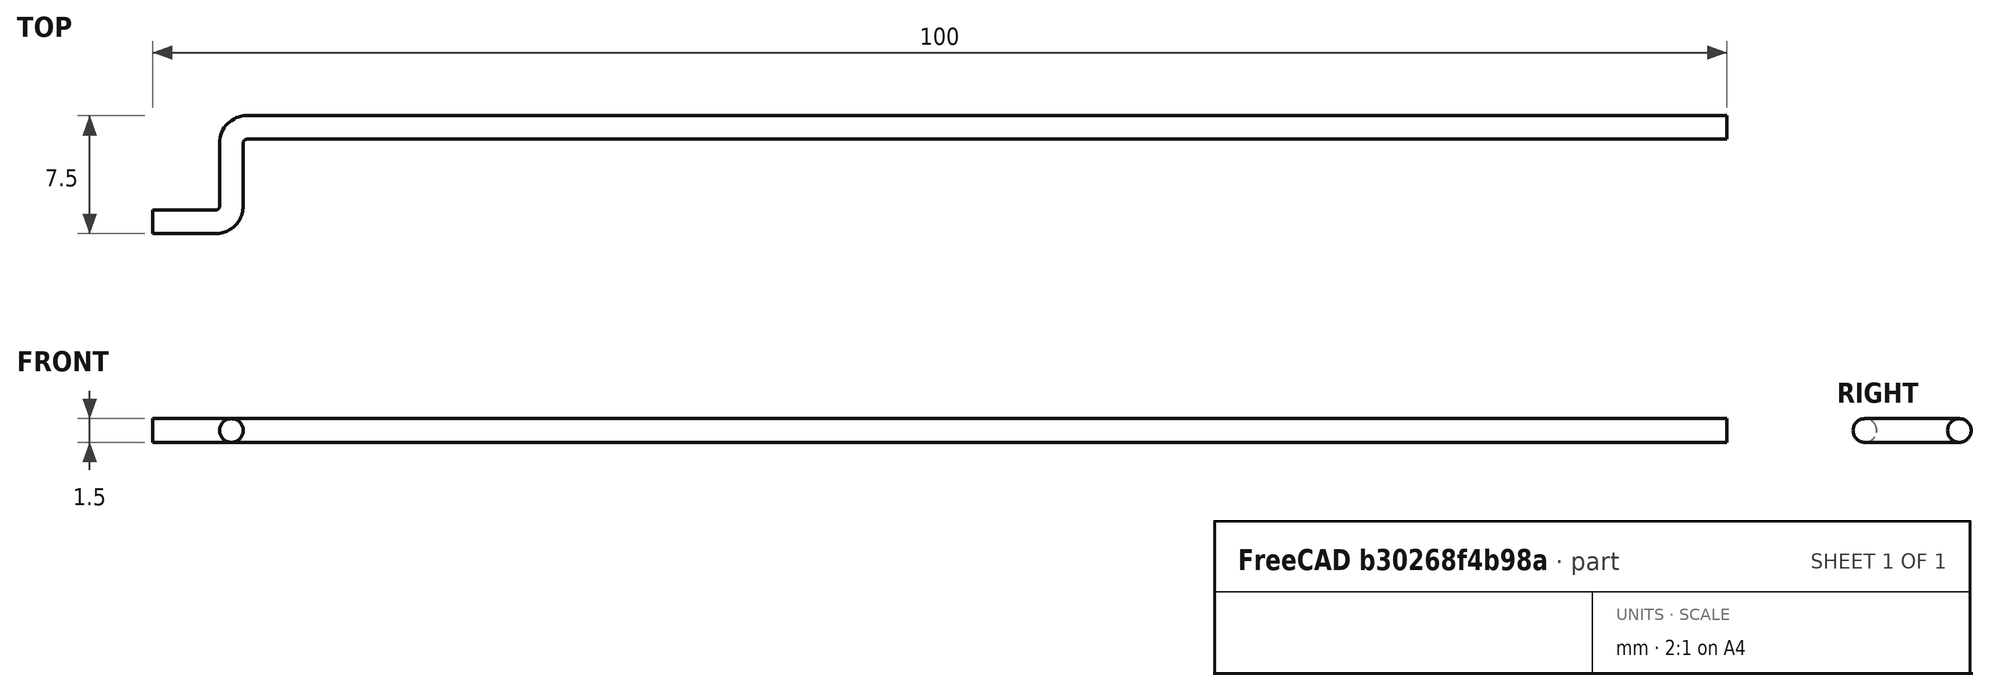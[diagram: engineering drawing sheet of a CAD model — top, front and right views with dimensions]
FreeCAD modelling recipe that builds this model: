
FCSTD DOCUMENT  (FreeCAD 0.15R4671 (Git))
Label: servo_rod_100mm
License: All rights reserved
LicenseURL: http://es.wikipedia.org/wiki/Todos_los_derechos_reservados
objects: Sketcher::SketchObject×2, Part::Sweep×1
note: 3 computed .brp shape members not serialized (recipe doc carries the construction recipe); baked Part::Feature solids carry a one-line shape summary decoded from their .brp

FEATURE [Sketcher::SketchObject] Sketch001  label="Sección"
  Placement = pos=(0,0,0) rot=(0.57735,0.57735,0.57735;2.0944rad)
  sketch-geometry (1):
    g0: Circle CenterX=0 CenterY=0 CenterZ=0 NormalX=0 NormalY=0 NormalZ=1 Radius=0.75
  constraints (2):
    c: Coincident(g0,g-1)
    c: Radius(g0) = 0.75
FEATURE [Sketcher::SketchObject] Sketch  label="Línea Varilla"
  sketch-geometry (5):
    g0: LineSegment StartX=0 StartY=0 StartZ=0 EndX=4 EndY=0 EndZ=0
    g1: LineSegment StartX=5 StartY=1 StartZ=0 EndX=5 EndY=5 EndZ=0
    g2: LineSegment StartX=6 StartY=6 StartZ=0 EndX=100 EndY=6 EndZ=0
    g3: ArcOfCircle CenterX=4 CenterY=1 CenterZ=0 NormalX=0 NormalY=0 NormalZ=1 Radius=1 StartAngle=4.71239 EndAngle=6.28319
    g4: ArcOfCircle CenterX=6 CenterY=5 CenterZ=0 NormalX=0 NormalY=0 NormalZ=1 Radius=1 StartAngle=1.5708 EndAngle=3.14159
  constraints (13):
    c: Coincident(g-1,g0)
    c: Horizontal(g0)
    c: Vertical(g1)
    c: Horizontal(g2)
    c: Tangent(g1,g3) = -1.5708
    c: Tangent(g0,g3) = -1.5708
    c: Tangent(g2,g4) = 1.5708
    c: Tangent(g1,g4) = 1.5708
    c: DistanceX(g-1,g0) = 4
    c: DistanceY(g1,g1) = -4
    c: DistanceX(g1,g0) = -1
    c: DistanceX(g2,g1) = -1
    c: DistanceX(g2,g2) = 94
FEATURE [Part::Sweep] Sweep
  Frenet = false
  Sections = -> [Sketch001]
  Solid = true
  Spine = -> Sketch [Edge1,Edge2,Edge3,Edge4,Edge5]
  Transition = 1
